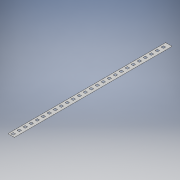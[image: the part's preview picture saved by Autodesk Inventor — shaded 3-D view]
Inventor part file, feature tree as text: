
AUTODESK INVENTOR PART (.ipt)
format: ipt  version: 2018 (Build 220112000, 112)  size: 210,944 bytes
history: native  units: in
note: dims shown in document units (in); Inventor stores cm internally (conversion verified against a paired STEP export)
features: extrude x2, sketch x2
ambient origin geometry x8: Origin, YZ Plane, XZ Plane, XY Plane, X Axis, Y Axis, Z Axis, Center Point
bodies: Solid1 (feature_tree)
feature tree (4):
  extrude  "Extrusion1"  Depth=12.4016in
  extrude  "Extrusion2"  Depth=0.18in
  sketch  "Sketch1"  dims[d0=0.5118in d1=12.4016in]
  sketch  "Sketch2"  dims[d2=0.0039in d3=0.0in d4=0.18in d5=0.18in d6=10.2362in d8=0.4724in d9=0.3937in d11=1.0in d13=0.0039in d14=0.0in]
